# Revit family: oventrop_hycocon-vpz_1061751-60rfa
name_source: partatom
category: Арматура трубопроводов
revit_build: Autodesk Revit 2017 (Build: 20160225_1515(x64)
units: mm (PartAtom-declared; Revit-internal decimal feet)

## family parameters
Всегда вертикально = Да
Заголовок OmniClass = Adjusting/Controlling Valves for Liquid Services
На основе рабочей плоскости = Нет
Номер OmniClass = 23.65.55.14.17
Общий = Нет
При загрузке вырезать с полостями = Нет
Размер круглого соединителя = Использовать радиус
Тип детали = Клапан - Вставляется

## types (6) — shared parameters
Angle = 55.00°
Article Description = Brass balancing valve both ports press connection
Article Type = Hycocon VPZ 10617
Bonnet = Color RGB 35-35-35
Brass = Color RGB 168-128-48
Custom = Нет
EMCS Version = 2.0
ETIM Article Class = EC011463
Family Version = 10.14
IFCExportAs = IfcValveType
IFCExportType = PRESSUREREDUCING
MEPcontent Class = VALVE_BALANCING
Manufacturer URL = http://www.oventrop.de
Pressure Drop = 0.0 Па
Product Line = Oventrop
Rad3 = 13 мм
Rad4 = 15 мм
Rad4_a = 12.426 мм
Rad5 = 10 мм
Revit Version = 2015
Группа модели = Hycocon VPZ 10617
Изготовитель = Oventrop
Описание = Brass balancing valve both ports press connection

## per-type parameters (varying)
| type | Bonnet_width | D | Diameter | Female_Port_Width | GTIN | H1 | H2 | Height | L1 | Length | Manufacturer Art. No. | NominalDiameter | Nut_Dimension | PressConnection_Dimension | Rad1 | Rad2 | SW2 | URL | e2 | t2 |
| DN 15-15 mm | 38 мм | 21 мм | 15 мм | 13.2 мм | 4026755343687 | 19 мм | 27.032 мм | 77 мм | 27.75 мм | 85 мм | 1061751 | 15.000 мм | 27 мм | 18 мм | 7.5 мм | 13.5 мм | 31.177 мм | www.stabiplan.com | 1.125 мм | 2.64 мм |
| DN 15-18 mm | 38 мм | 26 мм | 18 мм | 10.5 мм | 4026755343694 | 19 мм | 27.032 мм | 77 мм | 27.75 мм | 85 мм | 1061752 | 15.000 мм | 27 мм | 20 мм | 9 мм | 13.5 мм | 31.177 мм | www.stabiplan.com | 1.25 мм | 2.1 мм |
| DN 20-22 mm | 38 мм | 33 мм | 22 мм | 16.8 мм | 4026755343700 | 21 мм | 30.556 мм | 79 мм | 32 мм | 89 мм | 1061754 | 20.000 мм | 32 мм | 24 мм | 11 мм | 16 мм | 36.95 мм | www.stabiplan.com | 1.5 мм | 3.36 мм |
| DN 25-28 mm | 38 мм | 42 мм | 28 мм | 19.1 мм | 4026755343717 | 23 мм | 36.899 мм | 81 мм | 36.25 мм | 99 мм | 1061756 | 25.000 мм | 41 мм | 27 мм | 14 мм | 20.5 мм | 47.343 мм | www.stabiplan.com | 1.688 мм | 3.82 мм |
| DN 32-35 mm | 50 мм | 48 мм | 35 мм | 19.1 мм | 4026755343724 | 33 мм | 43.243 мм | 91 мм | 42.2 мм | 124 мм | 1061758 | 32.000 мм | 50 мм | 32 мм | 17.5 мм | 25 мм | 57.735 мм | www.stabiplan.com | 2 мм | 3.82 мм |
| DN 40-42 mm | 50 мм | 60 мм | 42 мм | 25.7 мм | 4026755343731 | 42 мм | 46.767 мм | 100 мм | 49 мм | 139 мм | 1061760 | 40.000 мм | 55 мм | 37.5 мм | 21 мм | 27.5 мм | 63.509 мм | http://file-system.ru | 2.344 мм | 5.14 мм |

## geometry (parser evidence)
native form markers: Blend x2, Sweep x5
no freeform markers — native parametric forms only
